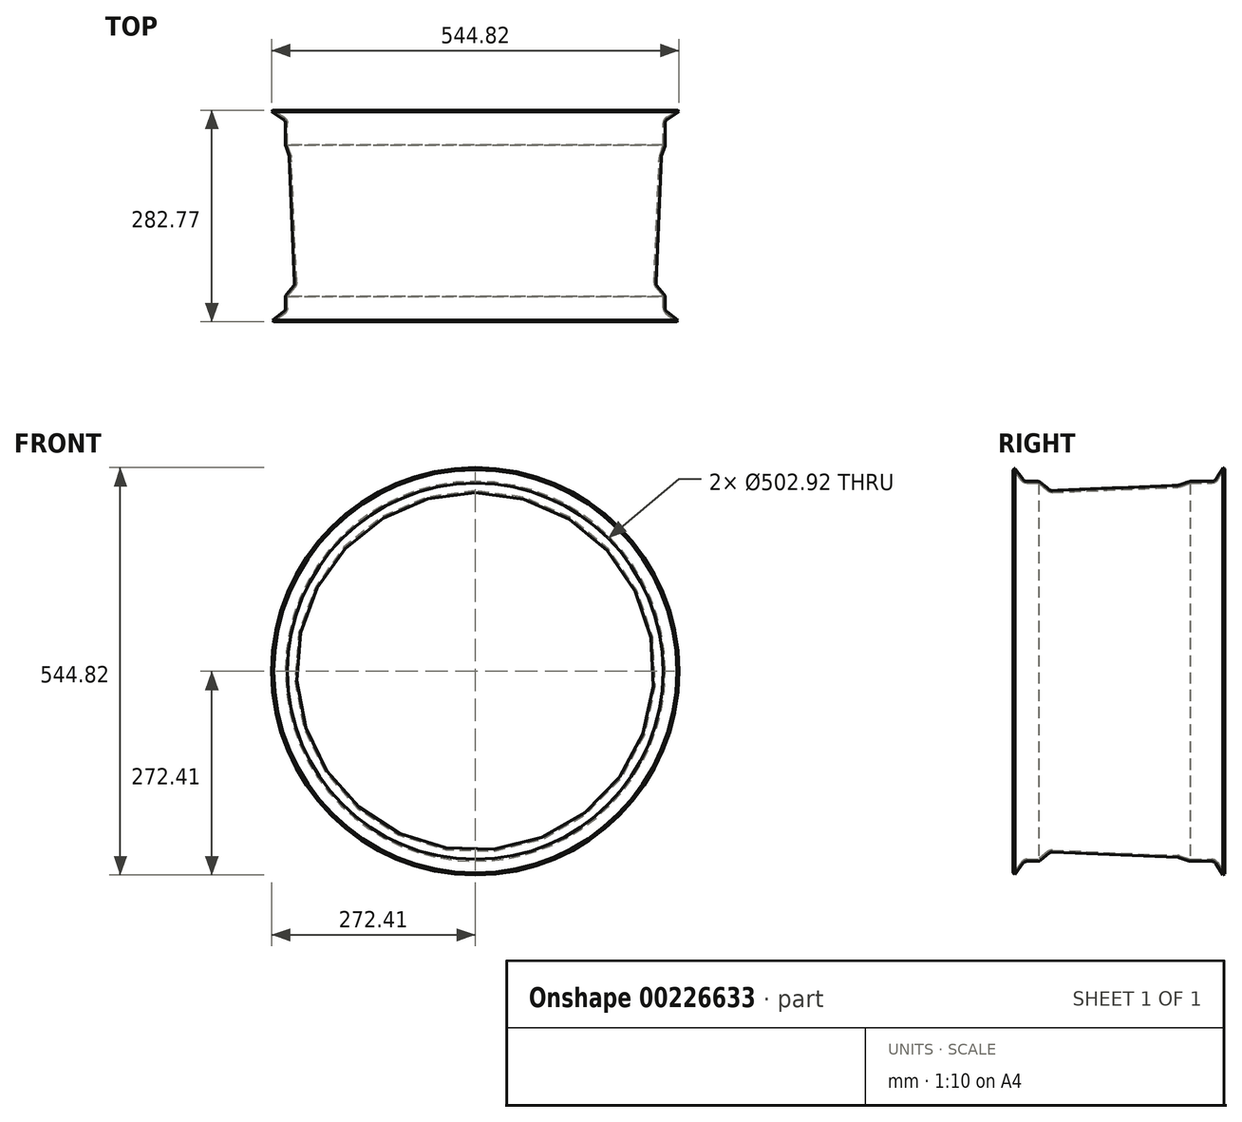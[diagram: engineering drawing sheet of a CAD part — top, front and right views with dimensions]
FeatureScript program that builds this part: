
annotation { "Feature Type Name" : "Feature", "Feature Type Description" : "" }
export const myFeature = defineFeature(function(context is Context, id is Id, definition is map)
    precondition{}
    {
        {
            var Q0;
            Q0=qCreatedBy(makeId("Right.planeOp"),FACE);
            var sketch = newSketch(context, id + "F0", { "sketchPlane" : qUnion([Q0])});
            skLineSegment(sketch, "E0", {"start": v(-123.86, 254) * mm, "end": v(-109.52, 254) * mm, "construction": true});
            skLineSegment(sketch, "E1", {"start": v(0, 0) * mm, "end": v(0, 254) * mm, "construction": true});
            skPoint(sketch, "E1.endSnap0", {"position": v(0, 254) * mm});
            skLineSegment(sketch, "E2", {"start": v(-140.14, 271.25) * mm, "end": v(-128.9, 256.5) * mm});
            skLineSegment(sketch, "E3", {"start": v(-105.46, 252.53) * mm, "end": v(-94.14, 243.13) * mm});
            skLineSegment(sketch, "E4", {"start": v(-89.81, 241.67) * mm, "end": v(77.91, 248.76) * mm});
            skLineSegment(sketch, "E5", {"start": v(79.7, 249.1) * mm, "end": v(93.05, 253.66) * mm});
            skLineSegment(sketch, "E6", {"start": v(95.1, 254) * mm, "end": v(123.47, 254) * mm});
            skLineSegment(sketch, "E7", {"start": v(128.86, 257) * mm, "end": v(138.45, 272.41) * mm});
            skPoint(sketch, "E8.visualSharp", {"position": v(-127, 254) * mm});
            skArc(sketch, "E8.filletArc", {"start": v(-128.9, 256.5) * mm, "mid": v(-126.67, 254.66) * mm, "end": v(-123.86, 254) * mm});
            skPoint(sketch, "E9.newPointA", {"position": v(127, 254) * mm});
            skArc(sketch, "E9.filletArc", {"start": v(-105.46, 252.53) * mm, "mid": v(-107.36, 253.62) * mm, "end": v(-109.52, 254) * mm});
            skPoint(sketch, "E10.visualSharp", {"position": v(-92.26, 241.57) * mm});
            skArc(sketch, "E10.filletArc", {"start": v(-94.14, 243.13) * mm, "mid": v(-92.11, 242) * mm, "end": v(-89.81, 241.67) * mm});
            skPoint(sketch, "E11.visualSharp", {"position": v(78.83, 248.8) * mm});
            skArc(sketch, "E11.filletArc", {"start": v(77.91, 248.76) * mm, "mid": v(78.82, 248.86) * mm, "end": v(79.7, 249.1) * mm});
            skPoint(sketch, "E12.visualSharp", {"position": v(94.04, 254) * mm});
            skArc(sketch, "E12.filletArc", {"start": v(95.1, 254) * mm, "mid": v(94.06, 253.91) * mm, "end": v(93.05, 253.66) * mm});
            skArc(sketch, "E13.filletArc", {"start": v(123.47, 254) * mm, "mid": v(126.56, 254.8) * mm, "end": v(128.86, 257) * mm});
            skSolve(sketch);
        }
        {
            var Q0;
            Q0=qCreatedBy(makeId("Right.planeOp"),FACE);
            var sketch = newSketch(context, id + "F1", { "sketchPlane" : qUnion([Q0])});
            skLineSegment(sketch, "E14.0", {"start": v(131.02, 255.65) * mm, "end": v(140.61, 271.07) * mm});
            skLineSegment(sketch, "E14.1", {"start": v(-108.14, 251.46) * mm, "end": v(-95.76, 241.18) * mm});
            skLineSegment(sketch, "E14.2", {"start": v(-123.86, 251.46) * mm, "end": v(-108.14, 251.46) * mm});
            skArc(sketch, "E14.3", {"start": v(-130.93, 254.96) * mm, "mid": v(-127.8, 252.38) * mm, "end": v(-123.86, 251.46) * mm});
            skLineSegment(sketch, "E14.4", {"start": v(-142.16, 269.7) * mm, "end": v(-130.93, 254.96) * mm});
            skArc(sketch, "E14.5", {"start": v(-95.76, 241.18) * mm, "mid": v(-92.93, 239.6) * mm, "end": v(-89.7, 239.13) * mm});
            skLineSegment(sketch, "E14.6", {"start": v(-89.7, 239.13) * mm, "end": v(78.02, 246.22) * mm});
            skArc(sketch, "E14.7", {"start": v(78.02, 246.22) * mm, "mid": v(79.29, 246.37) * mm, "end": v(80.52, 246.7) * mm});
            skLineSegment(sketch, "E14.8", {"start": v(80.52, 246.7) * mm, "end": v(94.47, 251.46) * mm});
            skLineSegment(sketch, "E14.9", {"start": v(94.47, 251.46) * mm, "end": v(123.47, 251.46) * mm});
            skArc(sketch, "E14.10", {"start": v(123.47, 251.46) * mm, "mid": v(127.79, 252.58) * mm, "end": v(131.02, 255.65) * mm});
            skLineSegment(sketch, "E15.0", {"start": v(-105.46, 252.53) * mm, "end": v(-94.14, 243.13) * mm});
            skLineSegment(sketch, "E15.1", {"start": v(-140.14, 271.25) * mm, "end": v(-128.9, 256.5) * mm});
            skArc(sketch, "E15.2", {"start": v(-128.9, 256.5) * mm, "mid": v(-126.67, 254.66) * mm, "end": v(-123.86, 254) * mm});
            skLineSegment(sketch, "E15.3", {"start": v(-123.86, 254) * mm, "end": v(-109.52, 254) * mm});
            skArc(sketch, "E15.4", {"start": v(-105.46, 252.53) * mm, "mid": v(-107.36, 253.62) * mm, "end": v(-109.52, 254) * mm});
            skPoint(sketch, "E15.5", {"position": v(-92.26, 241.57) * mm});
            skArc(sketch, "E15.6", {"start": v(-94.14, 243.13) * mm, "mid": v(-92.11, 242) * mm, "end": v(-89.81, 241.67) * mm});
            skLineSegment(sketch, "E15.7", {"start": v(-89.81, 241.67) * mm, "end": v(77.91, 248.76) * mm});
            skLineSegment(sketch, "E15.8", {"start": v(128.86, 257) * mm, "end": v(138.45, 272.41) * mm});
            skArc(sketch, "E15.9", {"start": v(123.47, 254) * mm, "mid": v(126.56, 254.8) * mm, "end": v(128.86, 257) * mm});
            skLineSegment(sketch, "E15.10", {"start": v(95.1, 254) * mm, "end": v(123.47, 254) * mm});
            skArc(sketch, "E15.11", {"start": v(95.1, 254) * mm, "mid": v(94.06, 253.91) * mm, "end": v(93.05, 253.66) * mm});
            skLineSegment(sketch, "E15.12", {"start": v(79.7, 249.1) * mm, "end": v(93.05, 253.66) * mm});
            skArc(sketch, "E15.13", {"start": v(77.91, 248.76) * mm, "mid": v(78.82, 248.86) * mm, "end": v(79.7, 249.1) * mm});
            skLineSegment(sketch, "E16", {"start": v(-140.14, 271.25) * mm, "end": v(-142.16, 269.7) * mm});
            skLineSegment(sketch, "E17", {"start": v(138.45, 272.41) * mm, "end": v(140.61, 271.07) * mm});
            skLineSegment(sketch, "E18", {"start": v(0, 0) * mm, "end": v(-132.17, 0) * mm, "construction": true});
            skSolve(sketch);
        }
        {
            var Q0;
            Q0=makeQuery(id+"F1.imprint","IMPRINT",FACE,{"disambiguationData":[TD([[makeQuery(id+"F1.imprint","IMPRINT",EDGE,{"derivedFrom":sQuery(id+"F1.wireOp",EDGE,"E14.0")}),1.0]])]});
            var Q1;
            Q1=qConstructionFilter(qBodyType(qCreatedBy(id+"F1",EDGE),BodyType.WIRE),ConstructionObject.NO);
            var Q2;
            Q2=sQuery(id+"F1.wireOp",EDGE,"E18");
            revolve(context, id + "F2", {"entities" : qUnion([Q0]), "surfaceEntities" : qUnion([Q1]), "axis" : qUnion([Q2]), "revolveType" : RevolveType.FULL});
        }
    });
